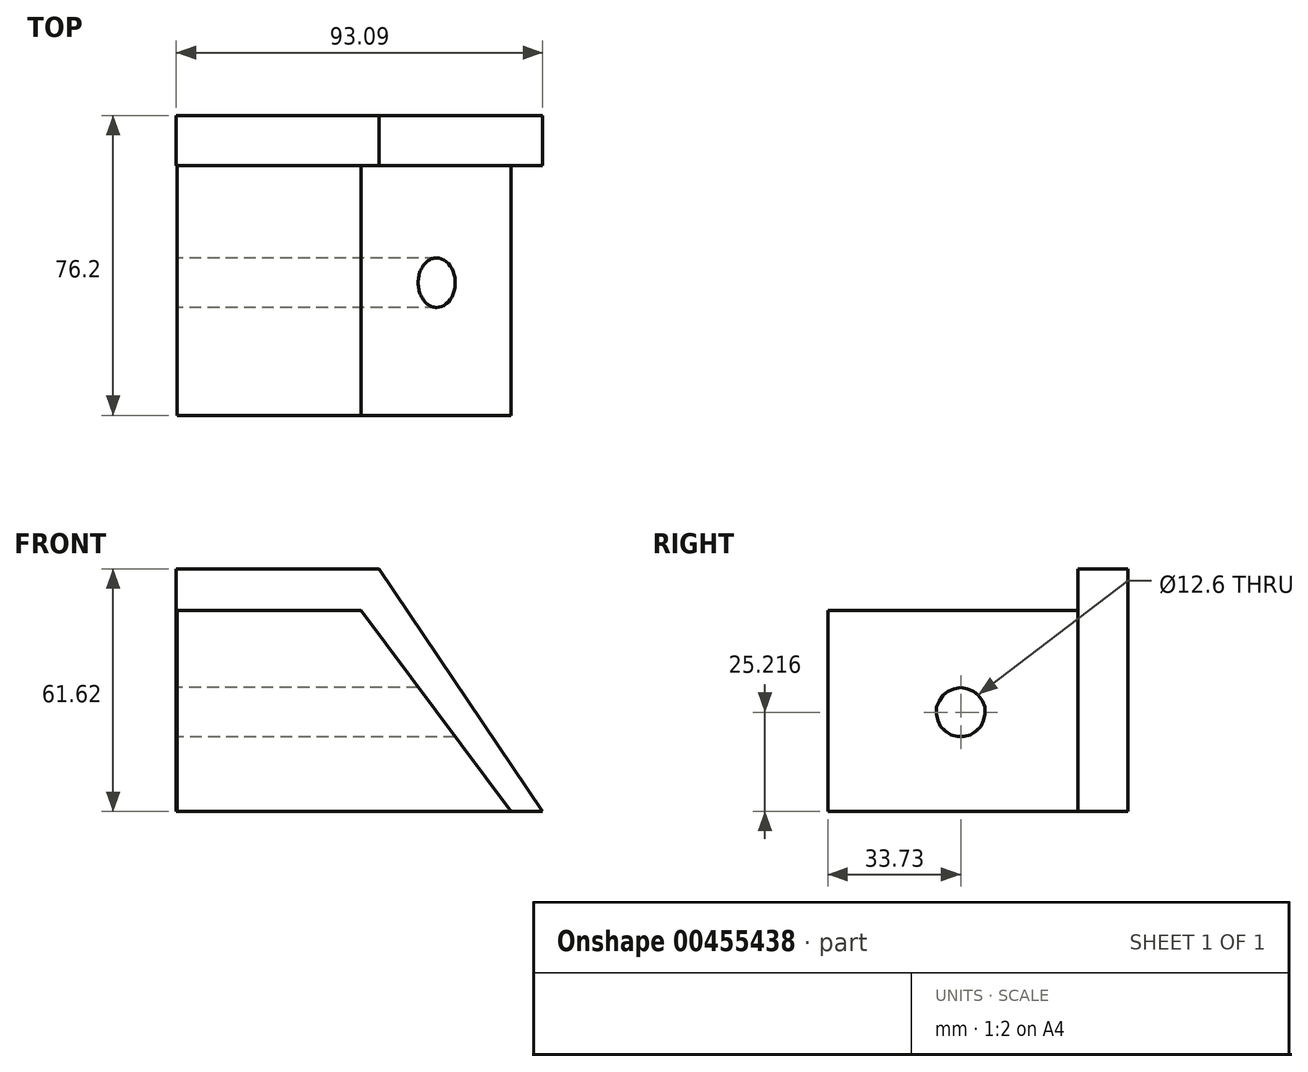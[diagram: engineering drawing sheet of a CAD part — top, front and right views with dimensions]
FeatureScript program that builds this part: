
annotation { "Feature Type Name" : "Feature", "Feature Type Description" : "" }
export const myFeature = defineFeature(function(context is Context, id is Id, definition is map)
    precondition{}
    {
        {
            var Q0;
            Q0=qCreatedBy(makeId("Front.planeOp"),FACE);
            var sketch = newSketch(context, id + "F0", { "sketchPlane" : qUnion([Q0])});
            skLineSegment(sketch, "E0", {"start": v(0, 0) * mm, "end": v(-41.52, 61.62) * mm});
            skLineSegment(sketch, "E1", {"start": v(-41.52, 61.62) * mm, "end": v(-93.1, 61.62) * mm});
            skLineSegment(sketch, "E2", {"start": v(-93.1, 61.62) * mm, "end": v(-93.1, 0) * mm});
            skLineSegment(sketch, "E3", {"start": v(-93.1, 0) * mm, "end": v(0, 0) * mm});
            skSolve(sketch);
        }
        {
            var Q0;
            Q0 = qSketchRegion(id + "F0", true);
            extrude(context, id + "F1", {"entities" : qUnion([Q0]), "depth" : 12.7 * mm});
        }
        {
            var Q0;
            Q0=makeQuery(id+"F1.opExtrude","CAP_FACE",FACE,{"disambiguationData":[OSD([sQuery(id+"F0.wireOp",EDGE,"E0"),sQuery(id+"F0.wireOp",EDGE,"E1"),sQuery(id+"F0.wireOp",EDGE,"E2"),sQuery(id+"F0.wireOp",EDGE,"E3")])],"isStart":false});
            var sketch = newSketch(context, id + "F2", { "sketchPlane" : qUnion([Q0])});
            skLineSegment(sketch, "E4", {"start": v(-92.9, 0) * mm, "end": v(-92.9, 51) * mm});
            skLineSegment(sketch, "E5", {"start": v(-92.9, 51) * mm, "end": v(-46.18, 51) * mm});
            skLineSegment(sketch, "E6", {"start": v(-46.18, 51) * mm, "end": v(-8.07, 0) * mm});
            skLineSegment(sketch, "E7", {"start": v(-8.07, 0) * mm, "end": v(-92.9, 0) * mm});
            skSolve(sketch);
        }
        {
            var Q0;
            Q0 = qSketchRegion(id + "F2", true);
            extrude(context, id + "F3", {"entities" : qUnion([Q0]), "operationType" : NewBodyOperationType.ADD, "depth" : 63.5 * mm});
        }
        {
            var Q0;
            Q0=makeQuery(id+"F3.opExtrude","SWEPT_FACE",FACE,{"disambiguationData":[OSD([sQuery(id+"F2.wireOp",EDGE,"E4")])]});
            var sketch = newSketch(context, id + "F4", { "sketchPlane" : qUnion([Q0])});
            skCircle(sketch, "E8", {"center": v(42.47, 25.22) * mm, "radius": 6.3 * mm});
            skSolve(sketch);
        }
        {
            var Q0;
            Q0 = qSketchRegion(id + "F4", true);
            extrude(context, id + "F5", {"entities" : qUnion([Q0]), "operationType" : NewBodyOperationType.REMOVE, "endBound" : BoundingType.THROUGH_ALL, "oppositeDirection" : true, "depth" : 25.4 * mm});
        }
    });
